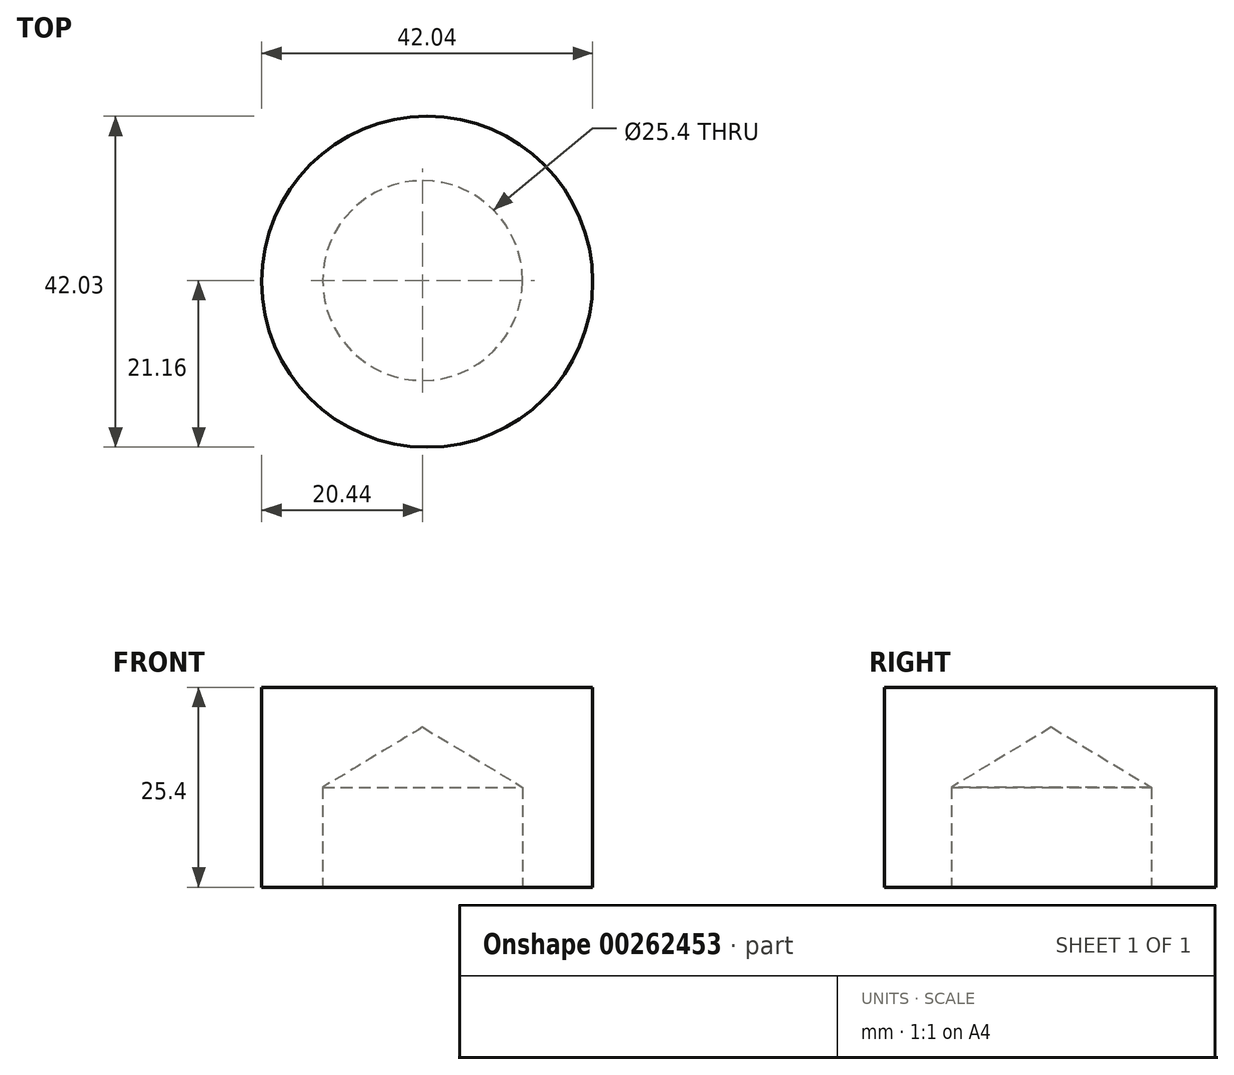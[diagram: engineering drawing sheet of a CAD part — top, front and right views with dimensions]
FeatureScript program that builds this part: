
annotation { "Feature Type Name" : "Feature", "Feature Type Description" : "" }
export const myFeature = defineFeature(function(context is Context, id is Id, definition is map)
    precondition{}
    {
        {
            var Q0;
            Q0=qCreatedBy(makeId("Top.planeOp"),FACE);
            var sketch = newSketch(context, id + "F0", { "sketchPlane" : qUnion([Q0])});
            skCircle(sketch, "E0", {"center": v(0.58, -0.15) * mm, "radius": 21.02 * mm});
            skSolve(sketch);
        }
        {
            var Q0;
            Q0=makeQuery(id+"F0.imprint","IMPRINT",FACE,{"disambiguationData":[TD([[makeQuery(id+"F0.imprint","IMPRINT",EDGE,{"derivedFrom":sQuery(id+"F0.wireOp",EDGE,"E0")}),1.0]])]});
            extrude(context, id + "F1", {"entities" : qUnion([Q0]), "depth" : 25.4 * mm});
        }
        {
            var Q0;
            Q0=qCreatedBy(makeId("Top.planeOp"),FACE);
            var sketch = newSketch(context, id + "F2", { "sketchPlane" : qUnion([Q0])});
            skLineSegment(sketch, "E1.bottom", {"start": v(0, 0) * mm, "end": v(20.4, 0) * mm});
            skLineSegment(sketch, "E1.top", {"start": v(0, -28.42) * mm, "end": v(20.4, -28.42) * mm});
            skLineSegment(sketch, "E1.left", {"start": v(0, 0) * mm, "end": v(0, -28.42) * mm});
            skLineSegment(sketch, "E1.right", {"start": v(20.4, 0) * mm, "end": v(20.4, -28.42) * mm});
            skSolve(sketch);
        }
        {
            var Q0;
            Q0=sQuery(id+"F2.wireOp",VERTEX,"E1.bottom.start");
            var Q1;
            Q1=makeQuery(id+"F1.opExtrude","SWEPT_BODY",BODY,{"disambiguationData":[OSD([sQuery(id+"F0.wireOp",EDGE,"E0")])]});
            hole(context, id + "F3", {"style" : HoleStyle.SIMPLE, "endStyle" : HoleEndStyle.BLIND, "oppositeDirection" : true, "holeDiameter" : 25.4 * mm, "holeDepth" : 12.7 * mm, "tappedDepth" : 12.7 * mm, "tapClearance" : 3, "locations" : qUnion([Q0]), "scope" : qUnion([Q1])});
        }
    });
